# Revit family: Molior 1 Line + S - Generic
name_source: partatom
category: Lighting Fixtures
revit_build: Autodesk Revit Architecture 2014 (Build: 20130308_1515(x64)
units: mm (PartAtom-declared; Revit-internal decimal feet)

## types (8) — shared parameters
ArticleNumber = See URL hyperlink
AssetType = Moveable/Fixed
BSAB 96 = SNB.2
BallastsCELMAEnergyEfficiencyIndex = Class A1/A2
CCSClassCode = UAC
CCSClassName = Belysningsarmatur
CCSTopnode = L
Cassette Depth = 0 mm
Cassette Width = 0 mm
Clearance Zones = Yes
Clearance Zones Offset = 60 mm
Color Filter = 16777215
Colour = White
ControlGearPosition = Integrated
Description = 70-80-35 General Lighting Systems
Dimming Lamp Color Temperature Shift = <None>
DocumentReference = See URL hyperlink
Documentation = See URL hyperlink
Finish = Powder coated
Frame = Riegens_Steel_Powder coated white RAL901025
Glass = Riegens_Glass_opal
Glass Depth = 540 mm
Glass Displacement = 0 mm
HasProtectiveEarth = TRUE
Height 1 = 35 mm
IP_Code = IP20
IfcExportAs = IfcLightFixtureType
IfcExportType = NOTDEFINED
InsulationStandardClass = Class 1
InternalFuse = Only required in emergency versions
LampColourRenderingIndex = Ra>80 / Ra>90 on request
LampRating = 14W / 17W
LampType = LED
LightFixtureMountingType = Recessed
LightFixturePlacingType = Ceiling
LightSource = LED 3000K / 4000K
LuminairePowerFactor = >0,9
LuminaireType = Recessed Direct LED Luminaire
Manufacturer = Riegens A/S
ManufacturerURL = www.riegens.com
Material = Steel and optic from PMMA.
NominalVoltage = 220-240V
Optic = Direct Collimating TIR optic
PhaseReference = IEC recommendations
PhotometricPerformance = In accordance with BS EN 13032-1
ProductInformation = http://riegens.com
Tilt Angle = 90.00°
Total height with brackets = 100 mm
TotalWattage = Max. 16W / 19W
Uniclass 1.4 = JY73
Uniclass2 = Pr_70_70_49_43 Light-Emitting Diode (LED) Luminaires
Version = v.1.0

## per-type parameters (varying)
| type | BIMObjectName | Bracket for C ceilings | Frame Length | Frame Width | ModelReference | Molior line 1 | Molior line 1 S | Photometric Web File | Shape | Size | Void Molior 1 | Void Molior 1 - S |
| Molior 1 Line 600x600 SAS 130 | Molior 1 Line 600x600 SAS 130.rfa | No | 584 mm | 584 mm | Molior 1 Line 600x600 SAS 130 | Yes | No | Molior 1 line 14W 4000K Lens Clear.ies | Square | 584 x 584 x 35 mm | 2 mm | -2 mm |
| Molior 1 Line 600x600 C | Molior 1 Line 600x600 C.rfa | Yes | 599 mm | 599 mm | Molior 1 Line 600x600 C | Yes | No | Molior 1 line 14W 4000K Lens Clear.ies | Square | 599 x 599 x 100 mm | 2 mm | -2 mm |
| Molior 1 Line 625x625 C | Molior 1 Line 625x625 C.rfa | Yes | 624 mm | 624 mm | Molior 1 Line 625x625 C | Yes | No | Molior 1 line 14W 4000K Lens Clear.ies | Square | 624 x 624 x 100 mm | 2 mm | -2 mm |
| Molior 1 Line 600x600 TL | Molior 1 Line 600x600 TL.rfa | No | 595 mm | 595 mm | Molior 1 Line 600x600 TL | Yes | No | Molior 1 line 14W 4000K Lens Clear.ies | Square | 595 x 595 x 35 mm | 2 mm | -2 mm |
| Molior 1 Line 625x625 TL | Molior 1 Line 625x625 TL.rfa | No | 620 mm | 620 mm | Molior 1 Line 625x625 TL | Yes | No | Molior 1 line 14W 4000K Lens Clear.ies | Square | 620 x 620 x 35 mm | 2 mm | -2 mm |
| Molior 1 Line S 600x600 SAS 130 | Molior 1 Line S 600x600 SAS 130.rfa | No | 584 mm | 584 mm | Nolior 1 Line S 600x600 SAS 130 | No | Yes | Molior 1 line S 14W 4000K Lens Clear.ies | Square | 584 x 584 x 35 mm | -2 mm | 2 mm |
| Molior 1 Line S 600x600 TL | Molior 1 Line S 600x600 TL.rfa | No | 595 mm | 595 mm | Nolior 1 Line S 600x600 TL | No | Yes | Molior 1 line S 14W 4000K Lens Clear.ies | Square | 595 x 595 x 35 mm | -2 mm | 2 mm |
| Molior 1 Line 300x600 TL | Molior 1 Line 300x600 TL.rfa | No | 595 mm | 295 mm | Molior 1 Line 300x600 TL | Yes | No | Molior 1 line 14W 4000K Lens Clear.ies | Rectangle | 295 x 595 x 35 mm | 2 mm | -2 mm |

## geometry (parser evidence)
native form markers: Blend x92, Sweep x3
no freeform markers — native parametric forms only
